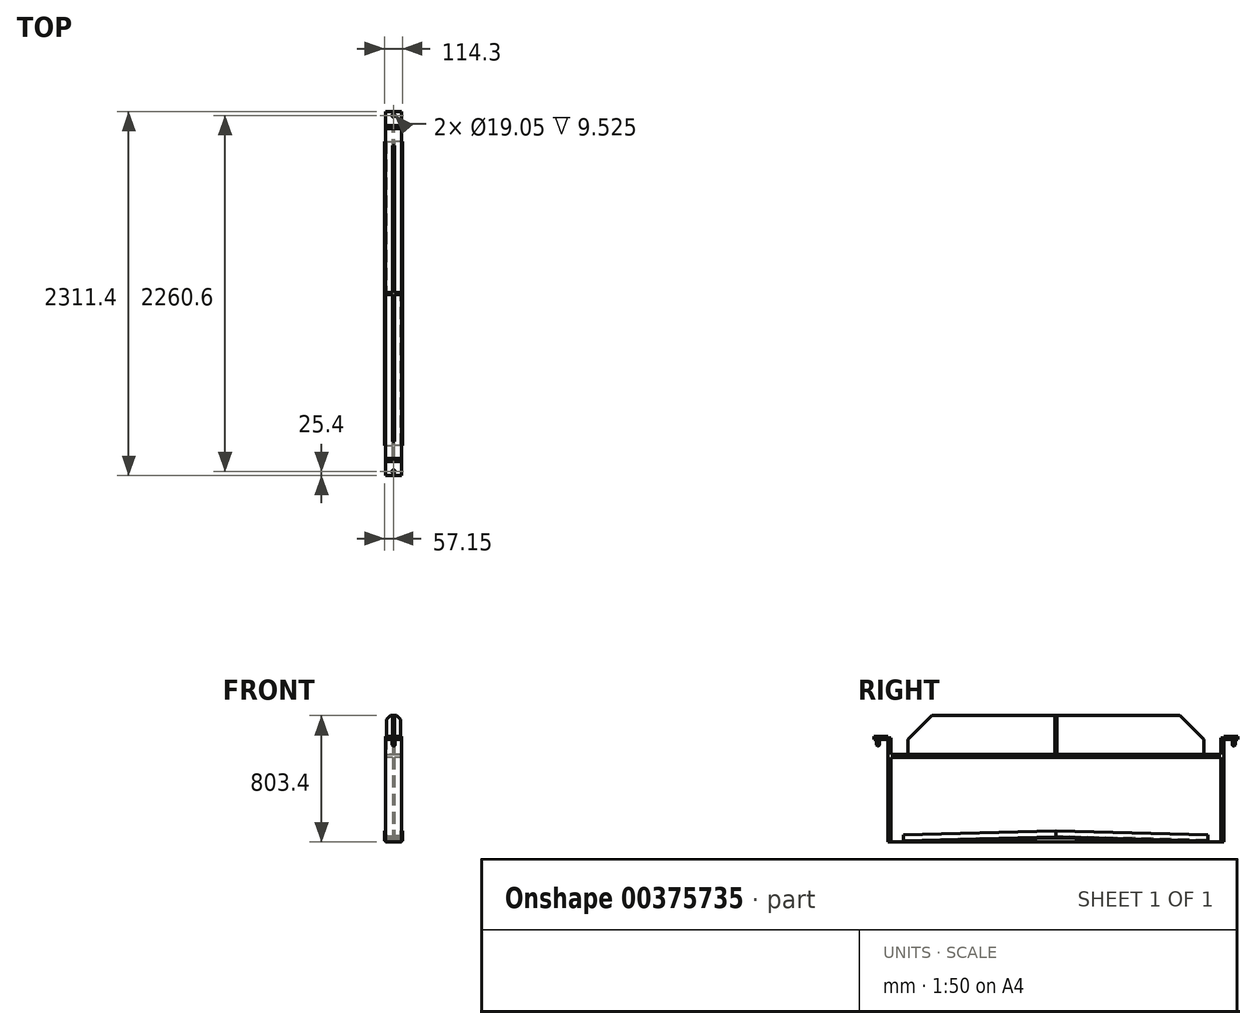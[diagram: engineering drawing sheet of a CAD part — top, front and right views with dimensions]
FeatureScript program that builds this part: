
annotation { "Feature Type Name" : "Feature", "Feature Type Description" : "" }
export const myFeature = defineFeature(function(context is Context, id is Id, definition is map)
    precondition{}
    {
        {
            var Q0;
            Q0=qCreatedBy(makeId("Right.planeOp"),FACE);
            var sketch = newSketch(context, id + "F0", { "sketchPlane" : qUnion([Q0])});
            skLineSegment(sketch, "E0", {"start": v(-1155.7, 0) * mm, "end": v(0, 0) * mm, "construction": true});
            skLineSegment(sketch, "E1", {"start": v(0, 991.09) * mm, "end": v(0, -891.64) * mm, "construction": true});
            skLineSegment(sketch, "E2.bottom", {"start": v(-1155.7, 0) * mm, "end": v(-1066.8, 0) * mm});
            skLineSegment(sketch, "E2.top", {"start": v(-1155.7, -19.05) * mm, "end": v(-1066.8, -19.05) * mm});
            skLineSegment(sketch, "E2.left", {"start": v(-1155.7, 0) * mm, "end": v(-1155.7, -19.05) * mm});
            skLineSegment(sketch, "E2.right", {"start": v(-1066.8, 0) * mm, "end": v(-1066.8, -19.05) * mm});
            skLineSegment(sketch, "E3.bottom", {"start": v(-1066.8, -9.53) * mm, "end": v(-1047.75, -9.53) * mm});
            skLineSegment(sketch, "E3.top", {"start": v(-1066.8, -669.93) * mm, "end": v(-1047.75, -669.93) * mm});
            skLineSegment(sketch, "E3.left", {"start": v(-1066.8, -9.52) * mm, "end": v(-1066.8, -669.93) * mm});
            skLineSegment(sketch, "E3.right", {"start": v(-1047.75, -9.52) * mm, "end": v(-1047.75, -669.93) * mm});
            skLineSegment(sketch, "E4", {"start": v(-1047.75, -669.93) * mm, "end": v(-358.85, -669.93) * mm, "construction": true});
            skLineSegment(sketch, "E5.0", {"start": v(-1047.75, -133.22) * mm, "end": v(-358.85, -133.22) * mm, "construction": true});
            skLineSegment(sketch, "E6.bottom", {"start": v(-1047.75, -133.22) * mm, "end": v(0, -133.22) * mm});
            skLineSegment(sketch, "E6.top", {"start": v(-1047.75, -114.17) * mm, "end": v(0, -114.17) * mm});
            skLineSegment(sketch, "E6.left", {"start": v(-1047.75, -133.22) * mm, "end": v(-1047.75, -114.17) * mm});
            skLineSegment(sketch, "E6.right", {"start": v(0, -133.22) * mm, "end": v(0, -114.17) * mm});
            skLineSegment(sketch, "E7.MirrorCS", {"start": v(1066.8, 0) * mm, "end": v(1066.8, -19.05) * mm});
            skLineSegment(sketch, "E8.MirrorCS", {"start": v(1066.8, -9.53) * mm, "end": v(1047.75, -9.53) * mm});
            skLineSegment(sketch, "E9.MirrorCS", {"start": v(1155.7, 0) * mm, "end": v(1066.8, 0) * mm});
            skLineSegment(sketch, "E10.MirrorCS", {"start": v(1155.7, -19.05) * mm, "end": v(1066.8, -19.05) * mm});
            skLineSegment(sketch, "E11.MirrorCS", {"start": v(1155.7, 0) * mm, "end": v(1155.7, -19.05) * mm});
            skLineSegment(sketch, "E12.MirrorCS", {"start": v(1066.8, -669.93) * mm, "end": v(1047.75, -669.93) * mm});
            skLineSegment(sketch, "E13.MirrorCS", {"start": v(1047.75, -133.22) * mm, "end": v(1047.75, -114.17) * mm});
            skLineSegment(sketch, "E14.MirrorCS", {"start": v(1047.75, -133.22) * mm, "end": v(358.85, -133.22) * mm, "construction": true});
            skLineSegment(sketch, "E15.MirrorCS", {"start": v(1155.7, 0) * mm, "end": v(0, 0) * mm, "construction": true});
            skLineSegment(sketch, "E16.MirrorCS", {"start": v(1047.75, -114.17) * mm, "end": v(0, -114.17) * mm});
            skLineSegment(sketch, "E17.MirrorCS", {"start": v(1047.75, -133.22) * mm, "end": v(0, -133.22) * mm});
            skLineSegment(sketch, "E18.MirrorCS", {"start": v(1066.8, -9.52) * mm, "end": v(1066.8, -669.93) * mm});
            skLineSegment(sketch, "E19.MirrorCS", {"start": v(1047.75, -9.52) * mm, "end": v(1047.75, -669.93) * mm});
            skLineSegment(sketch, "E20.MirrorCS", {"start": v(1047.75, -669.93) * mm, "end": v(358.85, -669.93) * mm, "construction": true});
            skSolve(sketch);
        }
        {
            var Q0;
            {var subQ3=sQuery(id+"F0.wireOp",EDGE,"E3.bottom");Q0=makeQuery(id+"F0.imprint","IMPRINT",FACE,{"disambiguationData":[TD([[makeQuery(id+"F0.imprint","IMPRINT",EDGE,{"derivedFrom":subQ3}),-1.0]])]});}
            var Q1;
            Q1=makeQuery(id+"F0.imprint","IMPRINT",FACE,{"disambiguationData":[TD([[makeQuery(id+"F0.imprint","IMPRINT",EDGE,{"derivedFrom":sQuery(id+"F0.wireOp",EDGE,"E2.bottom")}),-1.0]])]});
            var Q2;
            Q2=makeQuery(id+"F0.imprint","IMPRINT",FACE,{"disambiguationData":[TD([[makeQuery(id+"F0.imprint","IMPRINT",EDGE,{"derivedFrom":sQuery(id+"F0.wireOp",EDGE,"E6.bottom")}),1.0]])]});
            var Q3;
            Q3=makeQuery(id+"F0.imprint","IMPRINT",FACE,{"disambiguationData":[TD([[makeQuery(id+"F0.imprint","IMPRINT",EDGE,{"derivedFrom":sQuery(id+"F0.wireOp",EDGE,"E6.right")}),-1.0]])]});
            var Q4;
            {var subQ1=sQuery(id+"F0.wireOp",EDGE,"E8.MirrorCS");Q4=makeQuery(id+"F0.imprint","IMPRINT",FACE,{"disambiguationData":[TD([[makeQuery(id+"F0.imprint","IMPRINT",EDGE,{"derivedFrom":subQ1}),1.0]])]});}
            var Q5;
            {var subQ1=sQuery(id+"F0.wireOp",EDGE,"E7.MirrorCS");Q5=makeQuery(id+"F0.imprint","IMPRINT",FACE,{"disambiguationData":[TD([[makeQuery(id+"F0.imprint","IMPRINT",EDGE,{"derivedFrom":subQ1}),1.0]])]});}
            extrude(context, id + "F1", {"entities" : qUnion([Q0, Q1, Q2, Q3, Q4, Q5]), "endBound" : BoundingType.SYMMETRIC, "depth" : 101.6 * mm});
        }
        {
            var Q0;
            Q0=qCreatedBy(makeId("Right.planeOp"),FACE);
            var sketch = newSketch(context, id + "F2", { "sketchPlane" : qUnion([Q0])});
            skLineSegment(sketch, "E21.0", {"start": v(-1047.75, -133.22) * mm, "end": v(1047.75, -133.22) * mm, "construction": true});
            skLineSegment(sketch, "E22.0", {"start": v(1047.75, -133.22) * mm, "end": v(1047.75, -669.93) * mm, "construction": true});
            skLineSegment(sketch, "E23.bottom", {"start": v(-1047.75, -133.22) * mm, "end": v(1047.75, -133.22) * mm});
            skLineSegment(sketch, "E23.top", {"start": v(-1047.75, -669.93) * mm, "end": v(1047.75, -669.93) * mm});
            skLineSegment(sketch, "E23.left", {"start": v(-1047.75, -133.22) * mm, "end": v(-1047.75, -669.93) * mm});
            skLineSegment(sketch, "E23.right", {"start": v(1047.75, -133.22) * mm, "end": v(1047.75, -669.93) * mm});
            skSolve(sketch);
        }
        {
            var Q0;
            Q0 = qSketchRegion(id + "F2", true);
            extrude(context, id + "F3", {"entities" : qUnion([Q0]), "operationType" : NewBodyOperationType.ADD, "endBound" : BoundingType.SYMMETRIC, "depth" : 12.7 * mm});
        }
        {
            var Q0;
            Q0=makeQuery(id+"F1.opExtrude","SWEPT_FACE",FACE,{"disambiguationData":[OSD([sQuery(id+"F0.wireOp",EDGE,"E6.top"),sQuery(id+"F0.wireOp",EDGE,"E16.MirrorCS")])]});
            var sketch = newSketch(context, id + "F4", { "sketchPlane" : qUnion([Q0])});
            skLineSegment(sketch, "E24.bottom", {"start": v(-6.35, -939.8) * mm, "end": v(6.35, -939.8) * mm});
            skLineSegment(sketch, "E24.top", {"start": v(-6.35, 939.8) * mm, "end": v(6.35, 939.8) * mm});
            skLineSegment(sketch, "E24.left", {"start": v(-6.35, -939.8) * mm, "end": v(-6.35, 939.8) * mm});
            skLineSegment(sketch, "E24.right", {"start": v(6.35, -939.8) * mm, "end": v(6.35, 939.8) * mm});
            skPoint(sketch, "E24.middle", {"position": v(0, 0) * mm});
            skSolve(sketch);
        }
        {
            var Q0;
            Q0 = qSketchRegion(id + "F4", true);
            extrude(context, id + "F5", {"entities" : qUnion([Q0]), "operationType" : NewBodyOperationType.ADD, "depth" : 247.65 * mm});
        }
        {
            var Q0;
            Q0=makeQuery(id+"F5.opExtrude","CAP_EDGE",EDGE,{"disambiguationData":[OSD([sQuery(id+"F4.wireOp",EDGE,"E24.bottom")])],"isStart":false});
            var Q1;
            Q1=makeQuery(id+"F5.opExtrude","CAP_EDGE",EDGE,{"disambiguationData":[OSD([sQuery(id+"F4.wireOp",EDGE,"E24.top")])],"isStart":false});
            chamfer(context, id + "F6", {"entities" : qUnion([Q0, Q1]), "width" : 152.4 * mm, "tangentPropagation" : true});
        }
        {
            var Q0;
            Q0=makeQuery(id+"F1.opExtrude","SWEPT_FACE",FACE,{"disambiguationData":[OSD([sQuery(id+"F0.wireOp",EDGE,"E6.top"),sQuery(id+"F0.wireOp",EDGE,"E16.MirrorCS")])]});
            var sketch = newSketch(context, id + "F7", { "sketchPlane" : qUnion([Q0])});
            skLineSegment(sketch, "E25.bottom", {"start": v(-44.45, -6.35) * mm, "end": v(44.45, -6.35) * mm});
            skLineSegment(sketch, "E25.top", {"start": v(-44.45, 6.35) * mm, "end": v(44.45, 6.35) * mm});
            skLineSegment(sketch, "E25.left", {"start": v(-44.45, -6.35) * mm, "end": v(-44.45, 6.35) * mm});
            skLineSegment(sketch, "E25.right", {"start": v(44.45, -6.35) * mm, "end": v(44.45, 6.35) * mm});
            skPoint(sketch, "E25.middle", {"position": v(0, 0) * mm});
            skSolve(sketch);
        }
        {
            var Q0;
            Q0 = qSketchRegion(id + "F7", true);
            extrude(context, id + "F8", {"entities" : qUnion([Q0]), "operationType" : NewBodyOperationType.ADD, "depth" : 247.65 * mm});
        }
        {
            var Q0;
            Q0=makeQuery(id+"F8.opExtrude","CAP_EDGE",EDGE,{"disambiguationData":[OSD([sQuery(id+"F7.wireOp",EDGE,"E25.right")])],"isStart":false});
            var Q1;
            Q1=makeQuery(id+"F8.opExtrude","CAP_EDGE",EDGE,{"disambiguationData":[OSD([sQuery(id+"F7.wireOp",EDGE,"E25.left")])],"isStart":false});
            chamfer(context, id + "F9", {"entities" : qUnion([Q0, Q1]), "width" : 25.4 * mm, "tangentPropagation" : true});
        }
        {
            var Q0;
            Q0=makeQuery(id+"F1.opExtrude","SWEPT_FACE",FACE,{"disambiguationData":[OSD([sQuery(id+"F0.wireOp",EDGE,"E9.MirrorCS")])]});
            var sketch = newSketch(context, id + "F10", { "sketchPlane" : qUnion([Q0])});
            skLineSegment(sketch, "E26", {"start": v(-283.3, 0) * mm, "end": v(232.62, 0) * mm, "construction": true});
            skLineSegment(sketch, "E27", {"start": v(0, -1298.5) * mm, "end": v(0, 1285.13) * mm, "construction": true});
            skLineSegment(sketch, "E28.0", {"start": v(-283.3, 1130.3) * mm, "end": v(232.62, 1130.3) * mm, "construction": true});
            skPoint(sketch, "E29", {"position": v(0, 1130.3) * mm});
            skPoint(sketch, "E30.MirrorP", {"position": v(0, -1130.3) * mm});
            skSolve(sketch);
        }
        {
            var Q0;
            Q0=sQuery(id+"F10.wireOp",VERTEX,"E30.MirrorP");
            var Q1;
            Q1=sQuery(id+"F10.wireOp",VERTEX,"E29");
            var Q2;
            Q2=makeQuery(id+"F1.opExtrude","SWEPT_BODY",BODY,{"disambiguationData":[OSD([sQuery(id+"F0.wireOp",EDGE,"E2.bottom"),sQuery(id+"F0.wireOp",EDGE,"E2.top"),sQuery(id+"F0.wireOp",EDGE,"E2.left"),sQuery(id+"F0.wireOp",EDGE,"E2.right"),sQuery(id+"F0.wireOp",EDGE,"E3.bottom"),sQuery(id+"F0.wireOp",EDGE,"E3.top"),sQuery(id+"F0.wireOp",EDGE,"E3.left"),sQuery(id+"F0.wireOp",EDGE,"E3.right"),sQuery(id+"F0.wireOp",EDGE,"E6.bottom"),sQuery(id+"F0.wireOp",EDGE,"E6.top"),sQuery(id+"F0.wireOp",EDGE,"E7.MirrorCS"),sQuery(id+"F0.wireOp",EDGE,"E8.MirrorCS"),sQuery(id+"F0.wireOp",EDGE,"E9.MirrorCS"),sQuery(id+"F0.wireOp",EDGE,"E10.MirrorCS"),sQuery(id+"F0.wireOp",EDGE,"E11.MirrorCS"),sQuery(id+"F0.wireOp",EDGE,"E12.MirrorCS"),sQuery(id+"F0.wireOp",EDGE,"E16.MirrorCS"),sQuery(id+"F0.wireOp",EDGE,"E17.MirrorCS"),sQuery(id+"F0.wireOp",EDGE,"E18.MirrorCS"),sQuery(id+"F0.wireOp",EDGE,"E19.MirrorCS")])]});
            hole(context, id + "F11", {"style" : HoleStyle.SIMPLE, "endStyle" : HoleEndStyle.THROUGH, "holeDiameter" : 19.05 * mm, "isTappedThrough" : true, "tappedDepth" : 7.75 * mm, "tapClearance" : 3, "locations" : qUnion([Q0, Q1]), "scope" : qUnion([Q2])});
        }
        {
            var Q0;
            Q0=makeQuery(id+"F1.opExtrude","SWEPT_FACE",FACE,{"disambiguationData":[OSD([sQuery(id+"F0.wireOp",EDGE,"E2.bottom")])]});
            cPlane(context, id + "F12", {"entities" : qUnion([Q0]), "cplaneType" : CPlaneType.OFFSET, "offset" : 9.52 * mm, "oppositeDirection" : true, "width" : 152.4 * mm, "height" : 152.4 * mm});
        }
        {
            var Q0;
            Q0=qCreatedBy(id+"F12.planeOp",FACE);
            var sketch = newSketch(context, id + "F13", { "sketchPlane" : qUnion([Q0])});
            skCircle(sketch, "E31.0", {"center": v(0, -1130.3) * mm, "radius": 9.53 * mm});
            skSolve(sketch);
        }
        {
            var Q0;
            Q0 = qSketchRegion(id + "F13", true);
            extrude(context, id + "F14", {"entities" : qUnion([Q0]), "oppositeDirection" : true, "depth" : 50.8 * mm});
        }
        {
            var Q0;
            Q0=makeQuery(id+"F14.opExtrude","CAP_FACE",FACE,{"disambiguationData":[OSD([sQuery(id+"F13.wireOp",EDGE,"E31.0")])],"isStart":false});
            chamfer(context, id + "F15", {"entities" : qUnion([Q0]), "width" : 6.35 * mm, "tangentPropagation" : true});
        }
        {
            var Q0;
            Q0=makeQuery(id+"F14.opExtrude","SWEPT_BODY",BODY,{"disambiguationData":[OSD([sQuery(id+"F13.wireOp",EDGE,"E31.0")])]});
            var Q1;
            Q1=qCreatedBy(makeId("Front.planeOp"),FACE);
            mirror(context, id + "F16", {"operationType" : NewBodyOperationType.ADD, "entities" : qUnion([Q0]), "mirrorPlane" : qUnion([Q1])});
        }
        {
            var Q0;
            Q0=makeQuery(id+"F3.opExtrude","CAP_FACE",FACE,{"disambiguationData":[OSD([sQuery(id+"F2.wireOp",EDGE,"E23.bottom"),sQuery(id+"F2.wireOp",EDGE,"E23.top"),sQuery(id+"F2.wireOp",EDGE,"E23.left"),sQuery(id+"F2.wireOp",EDGE,"E23.right")])],"isStart":false});
            var sketch = newSketch(context, id + "F17", { "sketchPlane" : qUnion([Q0])});
            skLineSegment(sketch, "E32", {"start": v(0, 405.54) * mm, "end": v(0, -946.37) * mm, "construction": true});
            skLineSegment(sketch, "E33.0", {"start": v(-1047.75, -669.93) * mm, "end": v(1047.75, -669.93) * mm, "construction": true});
            skLineSegment(sketch, "E34.0", {"start": v(-1047.75, -644.53) * mm, "end": v(1047.75, -644.53) * mm, "construction": true});
            skLineSegment(sketch, "E35.0", {"start": v(-965.2, 405.54) * mm, "end": v(-965.2, -946.37) * mm, "construction": true});
            skLineSegment(sketch, "E36", {"start": v(-965.2, -669.93) * mm, "end": v(0, -644.53) * mm});
            skLineSegment(sketch, "E37.0", {"start": v(-965.53, -657.23) * mm, "end": v(-0.33, -631.83) * mm});
            skLineSegment(sketch, "E38", {"start": v(-0.33, -631.83) * mm, "end": v(0, -644.53) * mm});
            skLineSegment(sketch, "E39", {"start": v(-965.53, -657.23) * mm, "end": v(-965.2, -669.93) * mm});
            skSolve(sketch);
        }
        {
            var Q0;
            Q0 = qSketchRegion(id + "F17", true);
            extrude(context, id + "F18", {"entities" : qUnion([Q0]), "depth" : 38.1 * mm});
        }
        {
            var Q0;
            Q0=makeQuery(id+"F18.opExtrude","CAP_FACE",FACE,{"disambiguationData":[OSD([sQuery(id+"F17.wireOp",EDGE,"E36"),sQuery(id+"F17.wireOp",EDGE,"E37.0"),sQuery(id+"F17.wireOp",EDGE,"E38"),sQuery(id+"F17.wireOp",EDGE,"E39")])],"isStart":false});
            var sketch = newSketch(context, id + "F19", { "sketchPlane" : qUnion([Q0])});
            skLineSegment(sketch, "E40.0", {"start": v(-965.37, -663.58) * mm, "end": v(0, -638.17) * mm});
            skLineSegment(sketch, "E41.0", {"start": v(-966.37, -625.5) * mm, "end": v(0, -600.06) * mm});
            skLineSegment(sketch, "E42", {"start": v(-966.37, -625.5) * mm, "end": v(-965.37, -663.58) * mm});
            skLineSegment(sketch, "E43", {"start": v(0, -638.17) * mm, "end": v(0, -600.06) * mm});
            skPoint(sketch, "E44.orphan", {"position": v(0, -682.24) * mm});
            skSolve(sketch);
        }
        {
            var Q0;
            Q0 = qSketchRegion(id + "F19", true);
            extrude(context, id + "F20", {"entities" : qUnion([Q0]), "operationType" : NewBodyOperationType.ADD, "depth" : 12.7 * mm});
        }
        {
            var Q0;
            Q0=makeQuery(id+"F18.opExtrude","SWEPT_BODY",BODY,{"disambiguationData":[OSD([sQuery(id+"F17.wireOp",EDGE,"E36"),sQuery(id+"F17.wireOp",EDGE,"E37.0"),sQuery(id+"F17.wireOp",EDGE,"E38"),sQuery(id+"F17.wireOp",EDGE,"E39")])]});
            var Q1;
            Q1=qCreatedBy(makeId("Front.planeOp"),FACE);
            mirror(context, id + "F21", {"entities" : qUnion([Q0]), "mirrorPlane" : qUnion([Q1])});
        }
        {
            var Q0;
            Q0=makeQuery(id+"F18.opExtrude","SWEPT_BODY",BODY,{"disambiguationData":[OSD([sQuery(id+"F17.wireOp",EDGE,"E36"),sQuery(id+"F17.wireOp",EDGE,"E37.0"),sQuery(id+"F17.wireOp",EDGE,"E38"),sQuery(id+"F17.wireOp",EDGE,"E39")])]});
            var Q1;
            Q1=qCreatedBy(makeId("Right.planeOp"),FACE);
            mirror(context, id + "F22", {"entities" : qUnion([Q0]), "mirrorPlane" : qUnion([Q1])});
        }
        {
            var Q0;
            Q0=makeQuery(id+"F22.opPattern","COPY",BODY,{"derivedFrom":makeQuery(id+"F18.opExtrude","SWEPT_BODY",BODY,{"disambiguationData":[OSD([sQuery(id+"F17.wireOp",EDGE,"E36"),sQuery(id+"F17.wireOp",EDGE,"E37.0"),sQuery(id+"F17.wireOp",EDGE,"E38"),sQuery(id+"F17.wireOp",EDGE,"E39")])]}),"instanceName":"1"});
            var Q1;
            Q1=qCreatedBy(makeId("Front.planeOp"),FACE);
            mirror(context, id + "F23", {"entities" : qUnion([Q0]), "mirrorPlane" : qUnion([Q1])});
        }
    });
